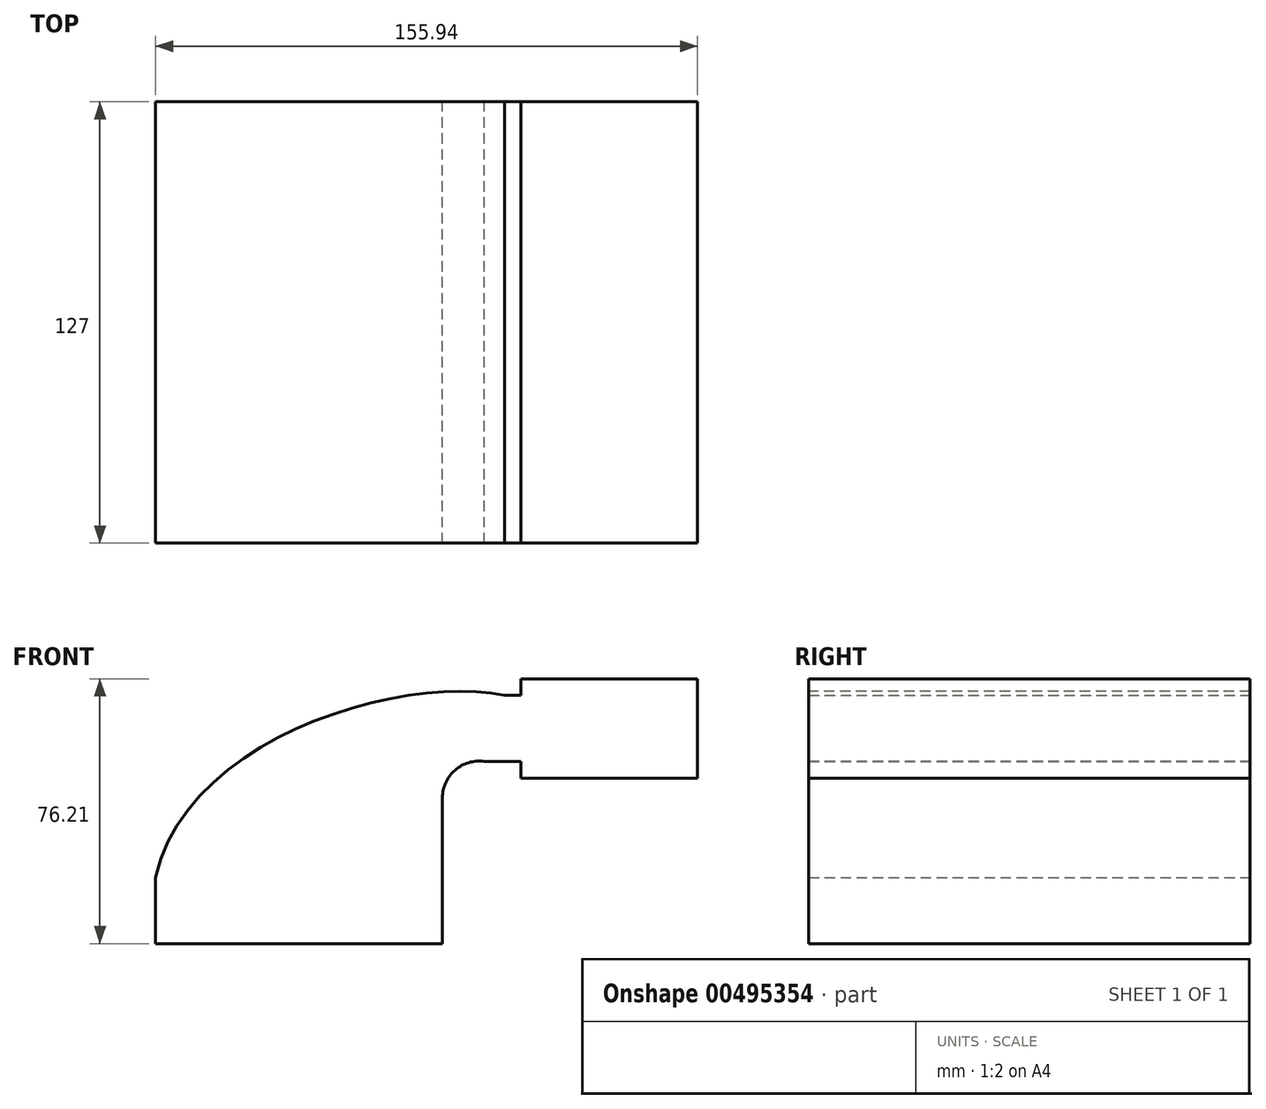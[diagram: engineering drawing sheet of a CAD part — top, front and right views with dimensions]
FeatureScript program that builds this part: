
annotation { "Feature Type Name" : "Feature", "Feature Type Description" : "" }
export const myFeature = defineFeature(function(context is Context, id is Id, definition is map)
    precondition{}
    {
        {
            var Q0;
            Q0=qCreatedBy(makeId("Front.planeOp"),FACE);
            var sketch = newSketch(context, id + "F0", { "sketchPlane" : qUnion([Q0])});
            skLineSegment(sketch, "E0.bottom", {"start": v(-41.28, 9.53) * mm, "end": v(41.28, 9.53) * mm});
            skLineSegment(sketch, "E0.top", {"start": v(-41.28, -9.53) * mm, "end": v(41.28, -9.53) * mm});
            skLineSegment(sketch, "E0.left", {"start": v(-41.28, 9.53) * mm, "end": v(-41.28, -9.53) * mm});
            skLineSegment(sketch, "E0.right", {"start": v(41.28, 9.53) * mm, "end": v(41.28, -9.53) * mm});
            skPoint(sketch, "E0.middle", {"position": v(0, 0) * mm});
            skLineSegment(sketch, "E1.bottom", {"start": v(63.86, 66.67) * mm, "end": v(114.66, 66.67) * mm});
            skLineSegment(sketch, "E1.top", {"start": v(63.86, 38.1) * mm, "end": v(114.66, 38.1) * mm});
            skLineSegment(sketch, "E1.left", {"start": v(63.86, 66.67) * mm, "end": v(63.86, 38.1) * mm});
            skLineSegment(sketch, "E1.right", {"start": v(114.66, 66.67) * mm, "end": v(114.66, 38.1) * mm});
            skPoint(sketch, "E1.middle", {"position": v(89.26, 52.39) * mm});
            skLineSegment(sketch, "E2", {"start": v(41.28, 9.53) * mm, "end": v(41.28, 32.45) * mm});
            skLineSegment(sketch, "E3", {"start": v(53.24, 42.88) * mm, "end": v(85.73, 42.88) * mm});
            skLineSegment(sketch, "E4.0", {"start": v(59.07, 61.93) * mm, "end": v(85.73, 61.93) * mm});
            skLineSegment(sketch, "E4.2", {"start": v(22.23, 9.53) * mm, "end": v(22.23, 27.58) * mm});
            skLineSegment(sketch, "E5", {"start": v(86.01, 38.1) * mm, "end": v(86.01, 66.67) * mm});
            skArc(sketch, "E6", {"start": v(41.28, 32.45) * mm, "mid": v(44.89, 40.38) * mm, "end": v(53.24, 42.88) * mm});
            skArc(sketch, "E7", {"start": v(22.23, 27.58) * mm, "mid": v(33.18, 52.77) * mm, "end": v(59.07, 61.93) * mm});
            skFitSpline(sketch, "E8", {"points": [v(-41.28, 9.53) * mm, v(59.07, 61.93) * mm], "startDerivative": vector(27.15, 123.17) * mm, "endDerivative": vector(84.44, -18.23) * mm});
            skSolve(sketch);
        }
        {
            var Q0;
            {var subQ6=sQuery(id+"F0.wireOp",EDGE,"E5");Q0=makeQuery(id+"F0.imprint","IMPRINT",FACE,{"disambiguationData":[TD([[makeQuery(id+"F0.imprint","IMPRINT",EDGE,{"derivedFrom":subQ6}),1.0]])]});}
            var Q1;
            {var subQ2=sQuery(id+"F0.wireOp",EDGE,"E4.2");Q1=makeQuery(id+"F0.imprint","IMPRINT",FACE,{"disambiguationData":[TD([[makeQuery(id+"F0.imprint","IMPRINT",EDGE,{"derivedFrom":subQ2}),1.0]])]});}
            var Q2;
            {var subQ4=sQuery(id+"F0.wireOp",EDGE,"E2");Q2=makeQuery(id+"F0.imprint","IMPRINT",FACE,{"disambiguationData":[TD([[makeQuery(id+"F0.imprint","IMPRINT",EDGE,{"derivedFrom":subQ4}),1.0]])]});}
            var Q3;
            {var subQ0=sQuery(id+"F0.wireOp",EDGE,"E1.right");Q3=makeQuery(id+"F0.imprint","IMPRINT",FACE,{"disambiguationData":[TD([[makeQuery(id+"F0.imprint","IMPRINT",EDGE,{"derivedFrom":subQ0}),-1.0]])]});}
            var Q4;
            Q4=makeQuery(id+"F0.imprint","IMPRINT",FACE,{"disambiguationData":[TD([[makeQuery(id+"F0.imprint","IMPRINT",EDGE,{"derivedFrom":sQuery(id+"F0.wireOp",EDGE,"E0.top")}),1.0]])]});
            extrude(context, id + "F1", {"entities" : qUnion([Q0, Q1, Q2, Q3, Q4]), "depth" : 127 * mm});
        }
    });
